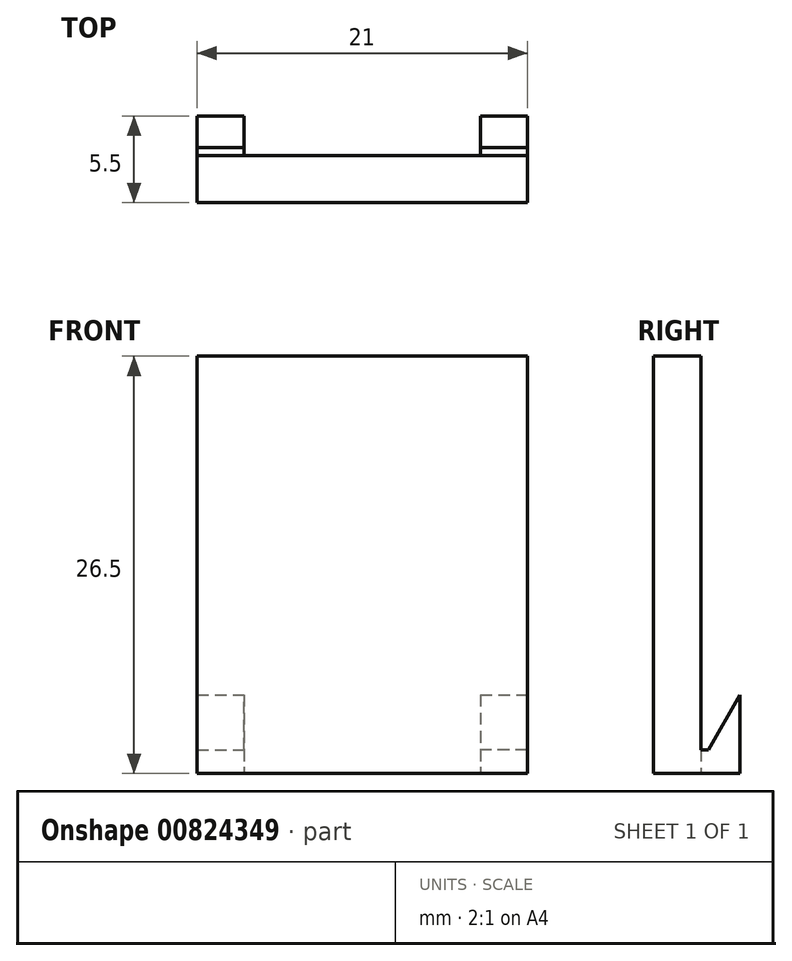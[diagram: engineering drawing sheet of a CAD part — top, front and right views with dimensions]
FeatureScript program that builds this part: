
annotation { "Feature Type Name" : "Feature", "Feature Type Description" : "" }
export const myFeature = defineFeature(function(context is Context, id is Id, definition is map)
    precondition{}
    {
        {
            var Q0;
            Q0=qCreatedBy(makeId("Top.planeOp"),FACE);
            var sketch = newSketch(context, id + "F0", { "sketchPlane" : qUnion([Q0])});
            skLineSegment(sketch, "E0", {"start": v(0, 0) * mm, "end": v(0, 5.5) * mm});
            skLineSegment(sketch, "E1", {"start": v(0, 5.5) * mm, "end": v(3, 5.5) * mm});
            skLineSegment(sketch, "E2", {"start": v(3, 5.5) * mm, "end": v(3, 3) * mm});
            skLineSegment(sketch, "E3", {"start": v(3, 3) * mm, "end": v(18, 3) * mm});
            skLineSegment(sketch, "E4", {"start": v(18, 3) * mm, "end": v(18, 5.5) * mm});
            skLineSegment(sketch, "E5", {"start": v(18, 5.5) * mm, "end": v(21, 5.5) * mm});
            skLineSegment(sketch, "E6", {"start": v(21, 5.5) * mm, "end": v(21, 0) * mm});
            skLineSegment(sketch, "E7", {"start": v(21, 0) * mm, "end": v(0, 0) * mm});
            skSolve(sketch);
        }
        {
            var Q0;
            Q0=makeQuery(id+"F0.imprint","IMPRINT",FACE,{"disambiguationData":[TD([[makeQuery(id+"F0.imprint","IMPRINT",EDGE,{"derivedFrom":sQuery(id+"F0.wireOp",EDGE,"E0")}),-1.0]])]});
            extrude(context, id + "F1", {"entities" : qUnion([Q0]), "depth" : 1.5 * mm, "offsetDistance" : 25.4 * mm});
        }
        {
            var Q0;
            Q0=makeQuery(id+"F1.opExtrude","CAP_FACE",FACE,{"disambiguationData":[OSD([sQuery(id+"F0.wireOp",EDGE,"E0"),sQuery(id+"F0.wireOp",EDGE,"E1"),sQuery(id+"F0.wireOp",EDGE,"E2"),sQuery(id+"F0.wireOp",EDGE,"E3"),sQuery(id+"F0.wireOp",EDGE,"E4"),sQuery(id+"F0.wireOp",EDGE,"E5"),sQuery(id+"F0.wireOp",EDGE,"E6"),sQuery(id+"F0.wireOp",EDGE,"E7")])],"isStart":false});
            var sketch = newSketch(context, id + "F2", { "sketchPlane" : qUnion([Q0])});
            skLineSegment(sketch, "E8.bottom", {"start": v(0, 5.5) * mm, "end": v(3, 5.5) * mm});
            skLineSegment(sketch, "E8.top", {"start": v(0, 3.5) * mm, "end": v(3, 3.5) * mm});
            skLineSegment(sketch, "E8.left", {"start": v(0, 5.5) * mm, "end": v(0, 3.5) * mm});
            skLineSegment(sketch, "E8.right", {"start": v(3, 5.5) * mm, "end": v(3, 3.5) * mm});
            skLineSegment(sketch, "E9.bottom", {"start": v(21, 5.5) * mm, "end": v(18, 5.5) * mm});
            skLineSegment(sketch, "E9.top", {"start": v(21, 3.5) * mm, "end": v(18, 3.5) * mm});
            skLineSegment(sketch, "E9.left", {"start": v(21, 5.5) * mm, "end": v(21, 3.5) * mm});
            skLineSegment(sketch, "E9.right", {"start": v(18, 5.5) * mm, "end": v(18, 3.5) * mm});
            skLineSegment(sketch, "E10.bottom", {"start": v(0, 0) * mm, "end": v(21, 0) * mm});
            skLineSegment(sketch, "E10.top", {"start": v(0, 3) * mm, "end": v(21, 3) * mm});
            skLineSegment(sketch, "E10.left", {"start": v(0, 0) * mm, "end": v(0, 3) * mm});
            skLineSegment(sketch, "E10.right", {"start": v(21, 0) * mm, "end": v(21, 3) * mm});
            skSolve(sketch);
        }
        {
            var Q0;
            Q0=makeQuery(id+"F2.imprint","IMPRINT",FACE,{"disambiguationData":[TD([[makeQuery(id+"F2.imprint","IMPRINT",EDGE,{"derivedFrom":sQuery(id+"F2.wireOp",EDGE,"E10.bottom")}),-1.0]])]});
            extrude(context, id + "F3", {"entities" : qUnion([Q0]), "operationType" : NewBodyOperationType.ADD, "depth" : 25 * mm, "offsetDistance" : 25.4 * mm});
        }
        {
            var Q0;
            Q0 = qSketchRegion(id + "F2", true);
            extrude(context, id + "F4", {"entities" : qUnion([Q0]), "operationType" : NewBodyOperationType.ADD, "depth" : 3.5 * mm, "offsetDistance" : 25.4 * mm});
        }
        {
            var Q0;
            Q0=makeQuery(id+"F4.boolean.opBoolean","MERGE",FACE,{"derivedFrom":[makeQuery(id+"F3.boolean.opBoolean","MERGE",FACE,{"derivedFrom":[makeQuery(id+"F1.opExtrude","SWEPT_FACE",FACE,{"disambiguationData":[OSD([sQuery(id+"F0.wireOp",EDGE,"E0")])]}),makeQuery(id+"F3.opExtrude","SWEPT_FACE",FACE,{"disambiguationData":[OSD([sQuery(id+"F2.wireOp",EDGE,"E10.left")])]})]}),makeQuery(id+"F4.opExtrude","SWEPT_FACE",FACE,{"disambiguationData":[OSD([sQuery(id+"F2.wireOp",EDGE,"E8.left")])]})]});
            var sketch = newSketch(context, id + "F5", { "sketchPlane" : qUnion([Q0])});
            skLineSegment(sketch, "E11", {"start": v(-5.5, 5) * mm, "end": v(-3.5, 1.5) * mm});
            skSolve(sketch);
        }
        {
            var Q0;
            Q0=makeQuery(id+"F5.imprint","IMPRINT",FACE,{"disambiguationData":[TD([[makeQuery(id+"F5.imprint","IMPRINT",EDGE,{"derivedFrom":sQuery(id+"F5.wireOp",EDGE,"E11")}),1.0]])]});
            extrude(context, id + "F6", {"entities" : qUnion([Q0]), "operationType" : NewBodyOperationType.REMOVE, "oppositeDirection" : true, "depth" : 127 * mm, "offsetDistance" : 25.4 * mm});
        }
    });
